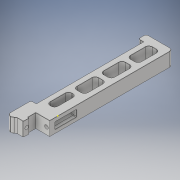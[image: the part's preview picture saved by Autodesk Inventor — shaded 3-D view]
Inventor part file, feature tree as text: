
AUTODESK INVENTOR PART (.ipt)
format: ipt  version: 2019 (Build 230136000, 136)  size: 1,079,296 bytes
history: native  units: mm
features: sketch x14, projected_geometry x13, extrude x12, fillet x11, chamfer x4, plane x2, hole x1
ambient origin geometry x8: Origin, YZ Plane, XZ Plane, XY Plane, X Axis, Y Axis, Z Axis, Center Point
bodies: Solid1 (feature_tree)
feature tree (57):
  extrude  "Extrusion1"  Depth=20.0mm
  plane  "Work Plane1"
  extrude  "Extrusion2"  Depth=7.5mm
  extrude  "Extrusion3"  Depth=7.5mm
  chamfer  "Chamfer1"  Distance=13.0mm
  fillet  "Fillet1"  Radius=1.25mm
  extrude  "Extrusion5"  Depth=20.0mm
  extrude  "Extrusion6"  TaperAngle=0.0deg  [1 undecoded]
  fillet  "Fillet2"  Radius=10.0mm
  extrude  "Extrusion8"  TaperAngle=0.0deg  [1 undecoded]
  fillet  "Fillet3"  [1 undecoded]
  hole  "Hole1"  [1 undecoded]
  extrude  "Extrusion9"  TaperAngle=0.0deg  [1 undecoded]
  fillet  "Fillet6"  Radius=6.5mm
  extrude  "Extrusion10"  Depth=10.0mm
  extrude  "Extrusion11"  Depth=10.0mm
  plane  "Work Plane2"
  extrude  "Extrusion15"  Depth=20.0mm
  extrude  "Extrusion14"  Depth=20.0mm
  fillet  "Fillet9"  Radius=20.0mm
  extrude  "Extrusion16"  Depth=20.0mm
  fillet  "Fillet10"  Radius=5.0mm
  chamfer  "Chamfer2"  Distance=5.0mm
  chamfer  "Chamfer3"  Distance=5.0mm
  fillet  "Fillet11"  Radius=10.0mm
  fillet  "Fillet12"  Radius=5.0mm
  fillet  "Fillet13"  Radius=5.0mm
  fillet  "Fillet14"  Radius=20.0mm
  fillet  "Fillet15"  Radius=4.15mm
  chamfer  "Chamfer4"  Distance=4.1mm
  sketch  "Sketch20"  dims[d33=2.5mm d34=3.4mm d35=6.0mm d36=6.5mm d37=3.0mm d38=90.0deg d39=8.0mm d40=20.594885mm d44=2.0mm d45=5.0mm d46=20.0mm d47=20.0mm d48=20.0mm d49=20.0mm d50=5.0mm d51=5.0mm d52=5.0mm d53=10.0mm d54=5.0mm d55=5.0mm d56=20.0mm d57=0.0mm d58=4.15mm d59=4.1mm d60=0.5mm d61=0.5mm d62=110.0mm d63=0.0mm d68=3.0mm d69=2.0mm d70=110.0mm d71=0.0mm d72=3.0mm d75=110.0mm d76=0.0mm d77=3.0mm d78=110.0mm d79=0.0mm d83=3.0mm d84=6.5mm d85=3.4mm d86=6.0mm d87=0.0mm d91=-5.0mm d92=6.0mm d95=20.0mm d96=0.0mm d97=20.0mm d98=0.0mm d101=3.0mm d102=3.0mm d103=1.25mm d104=0.0mm d105=0.5mm d106=0.2mm d107=10.0mm d108=45.0deg d109=0.2mm d110=10.0mm d111=45.0deg d112=0.25mm d113=0.25mm d114=0.25mm d115=0.25mm d116=0.25mm d117=0.2mm d118=10.0mm d119=45.0deg]
  sketch  "Sketch1"  dims[d0=20.0mm d1=100.0mm]
  sketch  "Sketch2"  dims[d2=7.5mm d3=30.0mm]
  projected_geometry  "Projected Loop1"
  sketch  "Sketch3"  dims[d4=5.0mm d5=7.5mm]
  projected_geometry  "Projected Loop2"
  sketch  "Sketch4"  dims[d6=0.0mm]
  projected_geometry  "Projected Loop3"
  sketch  "Sketch6"  dims[d7=7.5mm]
  projected_geometry  "Projected Loop5"
  sketch  "Sketch7"  dims[d8=10.0mm]
  projected_geometry  "Projected Loop6"
  projected_geometry  "Projected Loop7"
  sketch  "Sketch9"  dims[d9=6.0mm]
  projected_geometry  "Projected Loop9"
  sketch  "Sketch10"  dims[d10=6.0mm d11=13.0mm d12=0.0mm d14=1.25mm]
  projected_geometry  "Projected Loop10"
  sketch  "Sketch11"  dims[d15=5.5mm d17=20.0mm]
  projected_geometry  "Projected Loop11"
  sketch  "Sketch13"  dims[d18=20.0mm d19=0.0mm d20=10.0mm]
  projected_geometry  "Projected Loop13"
  sketch  "Sketch16"  dims[d21=10.0mm d22=0.0mm d23=0.0mm]
  projected_geometry  "Projected Loop16"
  sketch  "Sketch17"  dims[d24=20.0mm d25=0.0mm d26=20.0mm d27=0.0mm]
  projected_geometry  "Projected Loop17"
  sketch  "Sketch19"  dims[d28=0.5mm d29=2.0mm d30=45.0deg d31=0.0mm d32=6.5mm]
  projected_geometry  "Projected Loop18"
note: 5 required parameter values undecoded (feature->parameter linkage not recoverable at this tier; creation-order binding heuristic only, values carry confidence <= 0.55)
